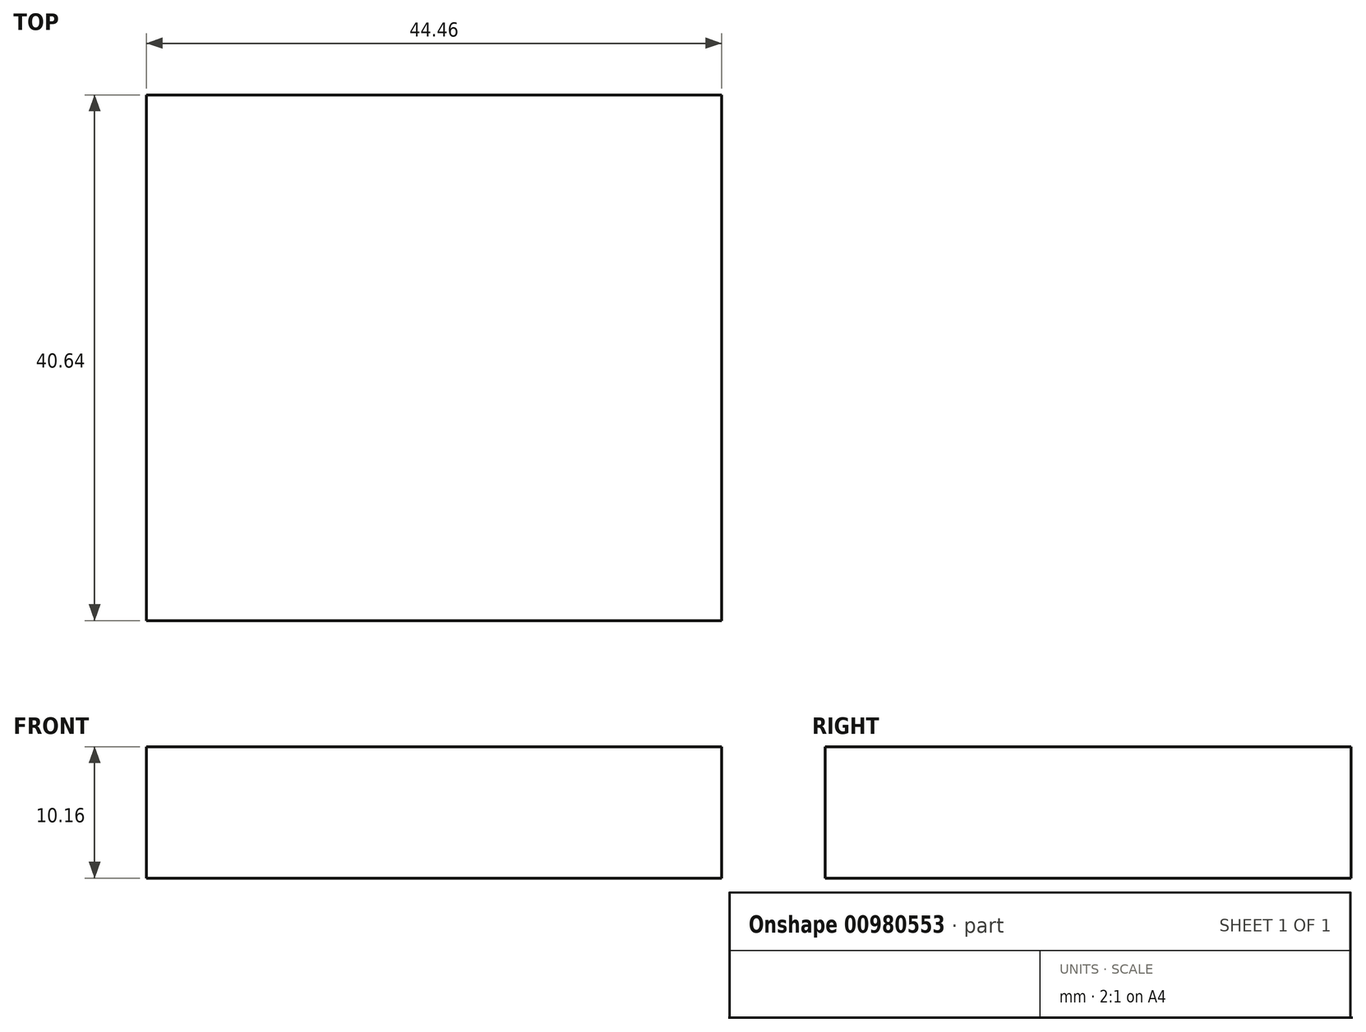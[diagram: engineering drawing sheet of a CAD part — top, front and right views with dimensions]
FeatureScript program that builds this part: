
annotation { "Feature Type Name" : "Feature", "Feature Type Description" : "" }
export const myFeature = defineFeature(function(context is Context, id is Id, definition is map)
    precondition{}
    {
        {
            var Q0;
            Q0=qCreatedBy(makeId("Top.planeOp"),FACE);
            var sketch = newSketch(context, id + "F0", { "sketchPlane" : qUnion([Q0])});
            skLineSegment(sketch, "E0.bottom", {"start": v(22.23, -20.32) * mm, "end": v(-22.23, -20.32) * mm});
            skLineSegment(sketch, "E0.top", {"start": v(22.23, 20.32) * mm, "end": v(-22.23, 20.32) * mm});
            skLineSegment(sketch, "E0.left", {"start": v(22.23, -20.32) * mm, "end": v(22.23, 20.32) * mm});
            skLineSegment(sketch, "E0.right", {"start": v(-22.23, -20.32) * mm, "end": v(-22.23, 20.32) * mm});
            skPoint(sketch, "E0.middle", {"position": v(0, 0) * mm});
            skSolve(sketch);
        }
        {
            var Q0;
            Q0=makeQuery(id+"F0.imprint","IMPRINT",FACE,{"disambiguationData":[TD([[makeQuery(id+"F0.imprint","IMPRINT",EDGE,{"derivedFrom":sQuery(id+"F0.wireOp",EDGE,"E0.bottom")}),-1.0]])]});
            extrude(context, id + "F1", {"entities" : qUnion([Q0]), "depth" : 10.16 * mm, "offsetDistance" : 25.4 * mm});
        }
    });
